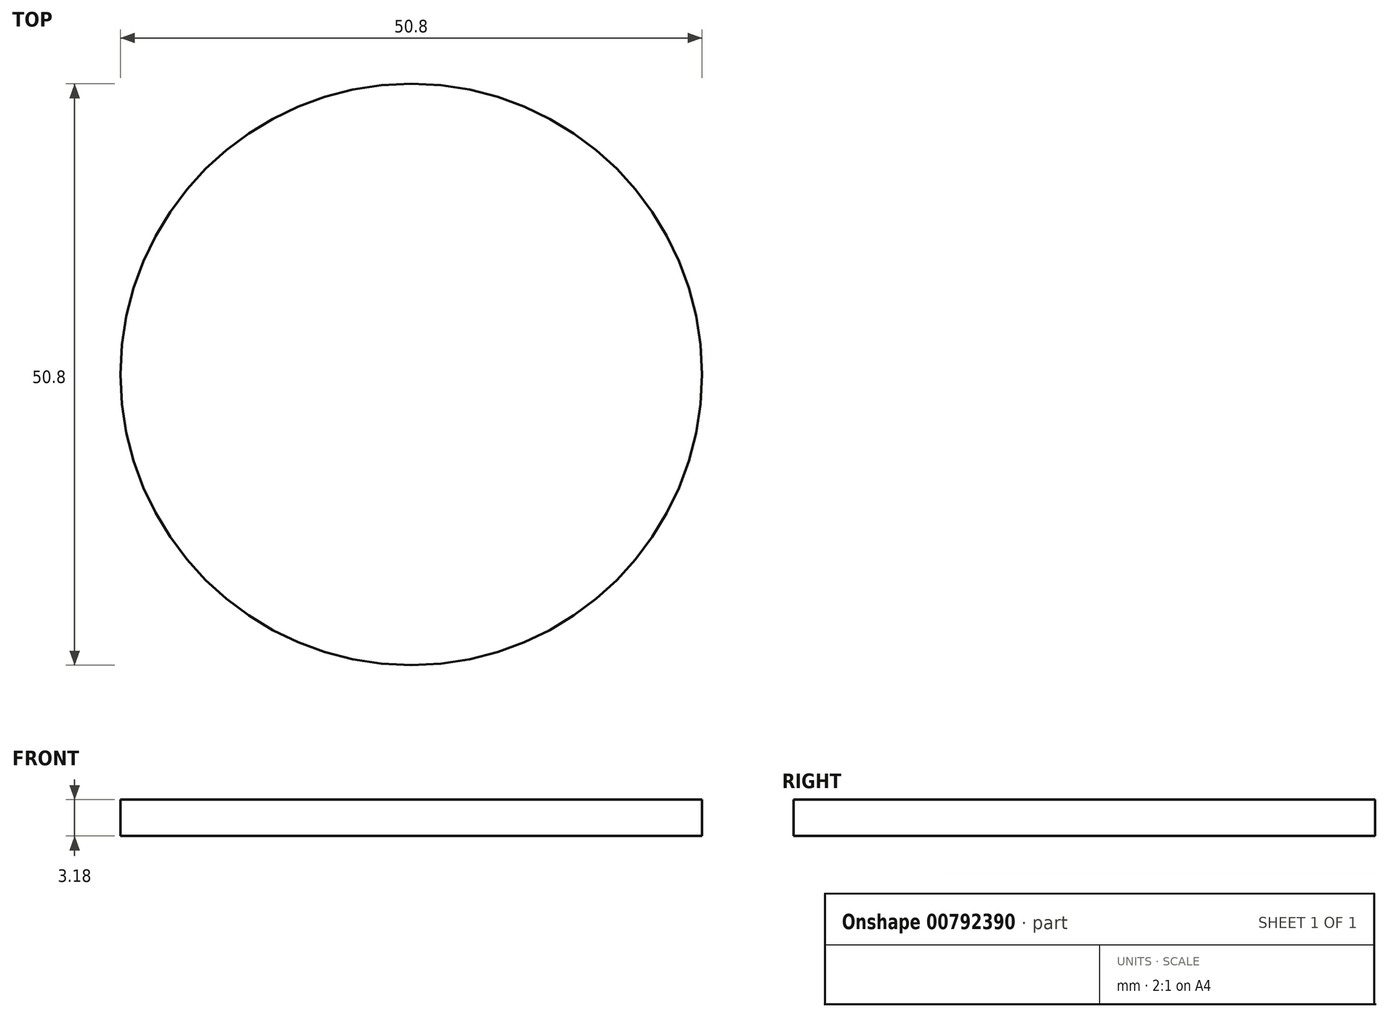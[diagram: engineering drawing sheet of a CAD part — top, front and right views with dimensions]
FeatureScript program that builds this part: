
annotation { "Feature Type Name" : "Feature", "Feature Type Description" : "" }
export const myFeature = defineFeature(function(context is Context, id is Id, definition is map)
    precondition{}
    {
        {
            var Q0;
            Q0=qCreatedBy(makeId("Top.planeOp"),FACE);
            var sketch = newSketch(context, id + "F0", { "sketchPlane" : qUnion([Q0])});
            skCircle(sketch, "E0", {"center": v(0, 0) * mm, "radius": 25.4 * mm});
            skSolve(sketch);
        }
        {
            var Q0;
            Q0 = qSketchRegion(id + "F0", true);
            extrude(context, id + "F1", {"entities" : qUnion([Q0]), "depth" : 3.17 * mm, "offsetDistance" : 25.4 * mm});
        }
    });
